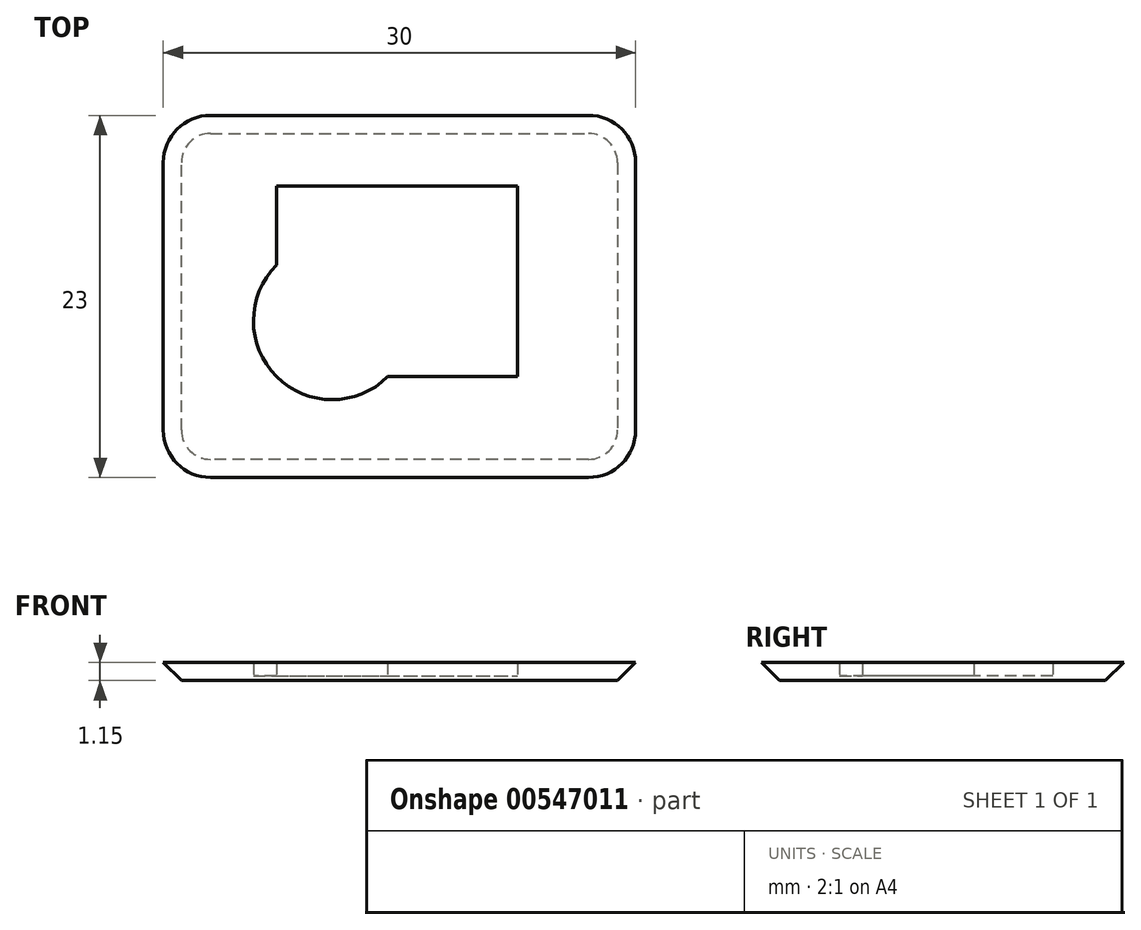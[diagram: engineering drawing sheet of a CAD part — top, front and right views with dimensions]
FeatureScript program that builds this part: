
annotation { "Feature Type Name" : "Feature", "Feature Type Description" : "" }
export const myFeature = defineFeature(function(context is Context, id is Id, definition is map)
    precondition{}
    {
        {
            var Q0;
            Q0=qCreatedBy(makeId("Top.planeOp"),FACE);
            var sketch = newSketch(context, id + "F0", { "sketchPlane" : qUnion([Q0])});
            skLineSegment(sketch, "E0.bottom", {"start": v(3, 0) * mm, "end": v(27, 0) * mm});
            skLineSegment(sketch, "E0.top", {"start": v(3, 23) * mm, "end": v(27, 23) * mm});
            skLineSegment(sketch, "E0.left", {"start": v(0, 3) * mm, "end": v(0, 20) * mm});
            skLineSegment(sketch, "E0.right", {"start": v(30, 3) * mm, "end": v(30, 20) * mm});
            skPoint(sketch, "E1.visualSharp", {"position": v(0, 0) * mm});
            skArc(sketch, "E1.filletArc", {"start": v(0, 3) * mm, "mid": v(0.88, 0.88) * mm, "end": v(3, 0) * mm});
            skPoint(sketch, "E2.visualSharp", {"position": v(0, 23) * mm});
            skArc(sketch, "E2.filletArc", {"start": v(3, 23) * mm, "mid": v(0.88, 22.12) * mm, "end": v(0, 20) * mm});
            skPoint(sketch, "E3.visualSharp", {"position": v(30, 23) * mm});
            skArc(sketch, "E3.filletArc", {"start": v(30, 20) * mm, "mid": v(29.12, 22.12) * mm, "end": v(27, 23) * mm});
            skPoint(sketch, "E4.visualSharp", {"position": v(30, 0) * mm});
            skArc(sketch, "E4.filletArc", {"start": v(27, 0) * mm, "mid": v(29.12, 0.88) * mm, "end": v(30, 3) * mm});
            skSolve(sketch);
        }
        {
            var Q0;
            Q0 = qSketchRegion(id + "F0", true);
            extrude(context, id + "F1", {"entities" : qUnion([Q0]), "depth" : 0.3 * mm, "offsetDistance" : 25 * mm});
        }
        {
            var Q0;
            Q0=makeQuery(id+"F1.opExtrude","CAP_FACE",FACE,{"disambiguationData":[OSD([sQuery(id+"F0.wireOp",EDGE,"E0.bottom"),sQuery(id+"F0.wireOp",EDGE,"E0.top"),sQuery(id+"F0.wireOp",EDGE,"E0.left"),sQuery(id+"F0.wireOp",EDGE,"E0.right")])],"isStart":false});
            var sketch = newSketch(context, id + "F2", { "sketchPlane" : qUnion([Q0])});
            skLineSegment(sketch, "E5.0", {"start": v(3, 23) * mm, "end": v(3, 23) * mm});
            skPoint(sketch, "E6.0", {"position": v(30, 11.5) * mm});
            skLineSegment(sketch, "E7.bottom", {"start": v(7.2, 18.5) * mm, "end": v(22.5, 18.5) * mm});
            skLineSegment(sketch, "E7.top", {"start": v(14.26, 6.4) * mm, "end": v(22.5, 6.4) * mm});
            skLineSegment(sketch, "E7.left", {"start": v(7.2, 18.5) * mm, "end": v(7.2, 13.49) * mm});
            skLineSegment(sketch, "E7.right", {"start": v(22.5, 18.5) * mm, "end": v(22.5, 6.4) * mm});
            skArc(sketch, "E8", {"start": v(7.2, 13.49) * mm, "mid": v(7.19, 6.41) * mm, "end": v(14.26, 6.4) * mm});
            skLineSegment(sketch, "E9.0", {"start": v(0, 3) * mm, "end": v(0, 20) * mm});
            skArc(sketch, "E10.0", {"start": v(0, 3) * mm, "mid": v(0.88, 0.88) * mm, "end": v(3, 0) * mm});
            skLineSegment(sketch, "E11.0", {"start": v(3, 0) * mm, "end": v(27, 0) * mm});
            skArc(sketch, "E12.0", {"start": v(27, 0) * mm, "mid": v(29.12, 0.88) * mm, "end": v(30, 3) * mm});
            skLineSegment(sketch, "E13.0", {"start": v(30, 3) * mm, "end": v(30, 20) * mm});
            skLineSegment(sketch, "E14.0", {"start": v(3, 23) * mm, "end": v(27, 23) * mm});
            skArc(sketch, "E15.0", {"start": v(30, 20) * mm, "mid": v(29.12, 22.12) * mm, "end": v(27, 23) * mm});
            skArc(sketch, "E16.0", {"start": v(3, 23) * mm, "mid": v(0.88, 22.12) * mm, "end": v(0, 20) * mm});
            skSolve(sketch);
        }
        {
            var Q0;
            Q0=makeQuery(id+"F2.imprint","IMPRINT",FACE,{"disambiguationData":[TD([[makeQuery(id+"F2.imprint","IMPRINT",EDGE,{"derivedFrom":sQuery(id+"F2.wireOp",EDGE,"E5.0")}),-1.0]])]});
            var Q1;
            Q1=makeQuery(id+"F2.imprint","IMPRINT",FACE,{"disambiguationData":[TD([[makeQuery(id+"F2.imprint","IMPRINT",EDGE,{"derivedFrom":sQuery(id+"F2.wireOp",EDGE,"E7.bottom")}),1.0]])]});
            extrude(context, id + "F3", {"entities" : qUnion([Q0, Q1]), "operationType" : NewBodyOperationType.ADD, "depth" : 0.85 * mm, "offsetDistance" : 25 * mm});
        }
        {
            var Q0;
            Q0=makeQuery(id+"F1.opExtrude","CAP_EDGE",EDGE,{"disambiguationData":[OSD([sQuery(id+"F0.wireOp",EDGE,"E0.bottom")])],"isStart":true});
            chamfer(context, id + "F4", {"entities" : qUnion([Q0]), "width" : 1.15 * mm, "tangentPropagation" : true});
        }
    });
